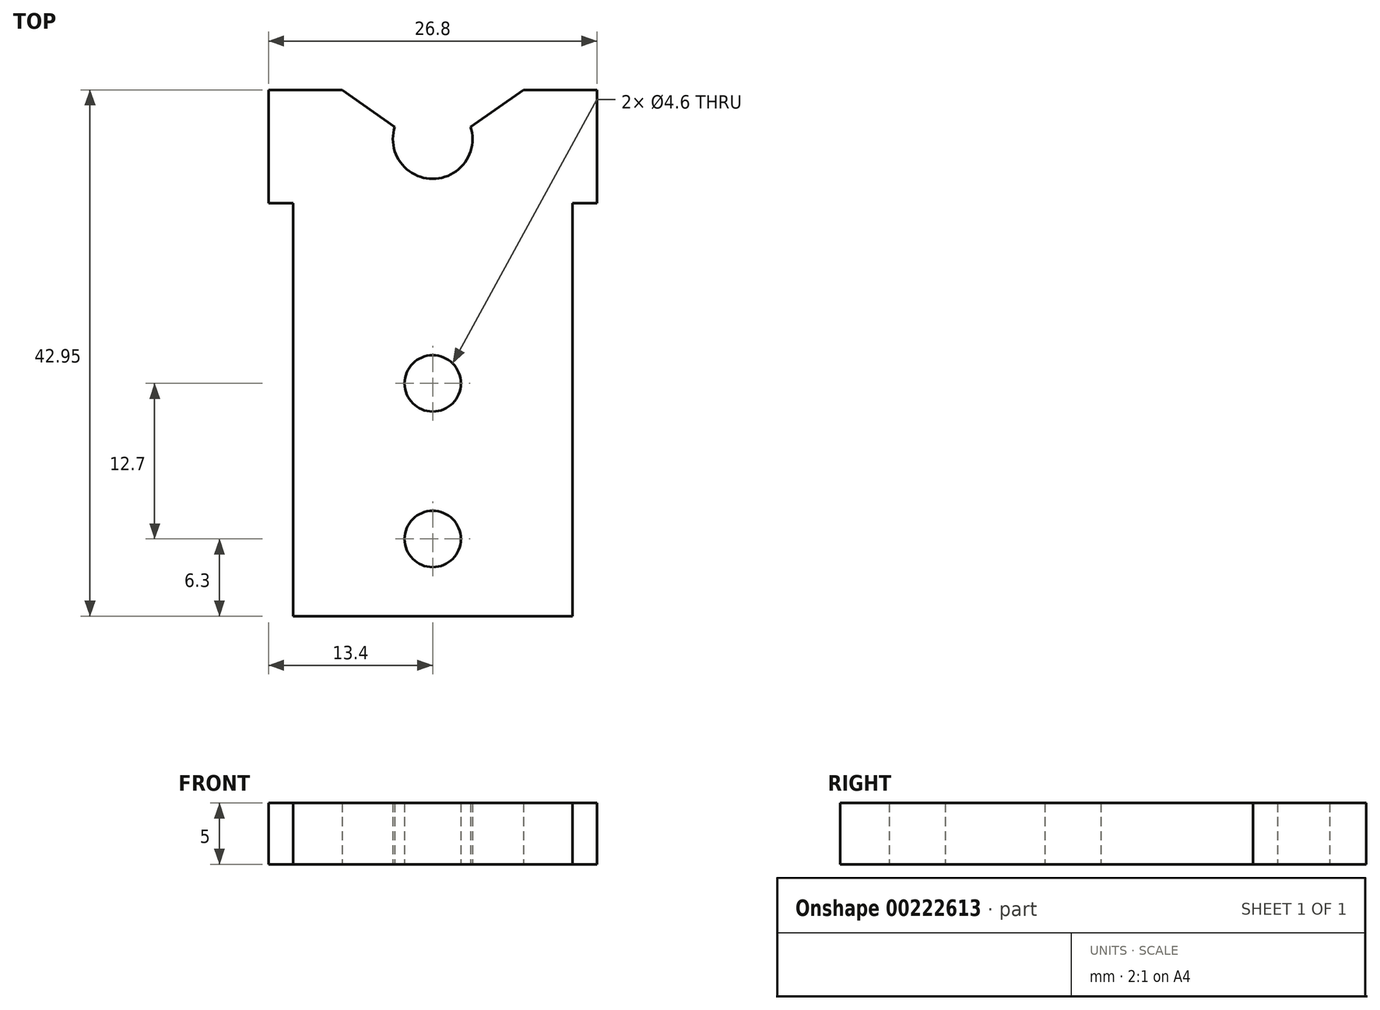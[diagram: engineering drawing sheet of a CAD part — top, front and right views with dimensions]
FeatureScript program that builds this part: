
annotation { "Feature Type Name" : "Feature", "Feature Type Description" : "" }
export const myFeature = defineFeature(function(context is Context, id is Id, definition is map)
    precondition{}
    {
        {
            var Q0;
            Q0=qCreatedBy(makeId("Top.planeOp"),FACE);
            var sketch = newSketch(context, id + "F0", { "sketchPlane" : qUnion([Q0])});
            skLineSegment(sketch, "E0", {"start": v(0, 0) * mm, "end": v(0, 42.95) * mm, "construction": true});
            skLineSegment(sketch, "E1", {"start": v(0, 42.95) * mm, "end": v(4, 42.95) * mm});
            skLineSegment(sketch, "E2", {"start": v(14.5, 39.95) * mm, "end": v(18.8, 42.95) * mm});
            skLineSegment(sketch, "E3", {"start": v(18.8, 42.95) * mm, "end": v(22.8, 42.95) * mm});
            skLineSegment(sketch, "E4", {"start": v(22.8, 42.95) * mm, "end": v(22.8, 0) * mm, "construction": true});
            skLineSegment(sketch, "E5", {"start": v(22.8, 0) * mm, "end": v(0, 0) * mm});
            skLineSegment(sketch, "E6", {"start": v(4, 42.95) * mm, "end": v(18.8, 42.95) * mm, "construction": true});
            skArc(sketch, "E7", {"start": v(8.3, 39.95) * mm, "mid": v(11.4, 35.7) * mm, "end": v(14.5, 39.95) * mm});
            skLineSegment(sketch, "E8", {"start": v(8.3, 39.95) * mm, "end": v(14.5, 39.95) * mm, "construction": true});
            skLineSegment(sketch, "E9", {"start": v(11.4, 39.95) * mm, "end": v(11.4, 0) * mm, "construction": true});
            skCircle(sketch, "E10", {"center": v(11.4, 19) * mm, "radius": 2.3 * mm});
            skCircle(sketch, "E11", {"center": v(11.4, 6.3) * mm, "radius": 2.3 * mm});
            skLineSegment(sketch, "E12", {"start": v(4, 42.95) * mm, "end": v(8.3, 39.95) * mm});
            skLineSegment(sketch, "E13", {"start": v(0, 33.7) * mm, "end": v(22.8, 33.7) * mm, "construction": true});
            skLineSegment(sketch, "E14", {"start": v(0, 0) * mm, "end": v(0, 33.7) * mm});
            skLineSegment(sketch, "E15", {"start": v(-2, 33.7) * mm, "end": v(-2, 42.95) * mm});
            skLineSegment(sketch, "E16", {"start": v(-2, 42.95) * mm, "end": v(0, 42.95) * mm});
            skLineSegment(sketch, "E17", {"start": v(22.8, 42.95) * mm, "end": v(24.8, 42.95) * mm});
            skLineSegment(sketch, "E18", {"start": v(24.8, 42.95) * mm, "end": v(24.8, 33.7) * mm});
            skLineSegment(sketch, "E19", {"start": v(24.8, 33.7) * mm, "end": v(22.8, 33.7) * mm});
            skLineSegment(sketch, "E20", {"start": v(22.8, 0) * mm, "end": v(22.8, 33.7) * mm});
            skLineSegment(sketch, "E21", {"start": v(-2, 33.7) * mm, "end": v(0, 33.7) * mm});
            skSolve(sketch);
        }
        {
            var Q0;
            Q0 = qSketchRegion(id + "F0", true);
            extrude(context, id + "F1", {"entities" : qUnion([Q0]), "depth" : 5 * mm});
        }
    });
